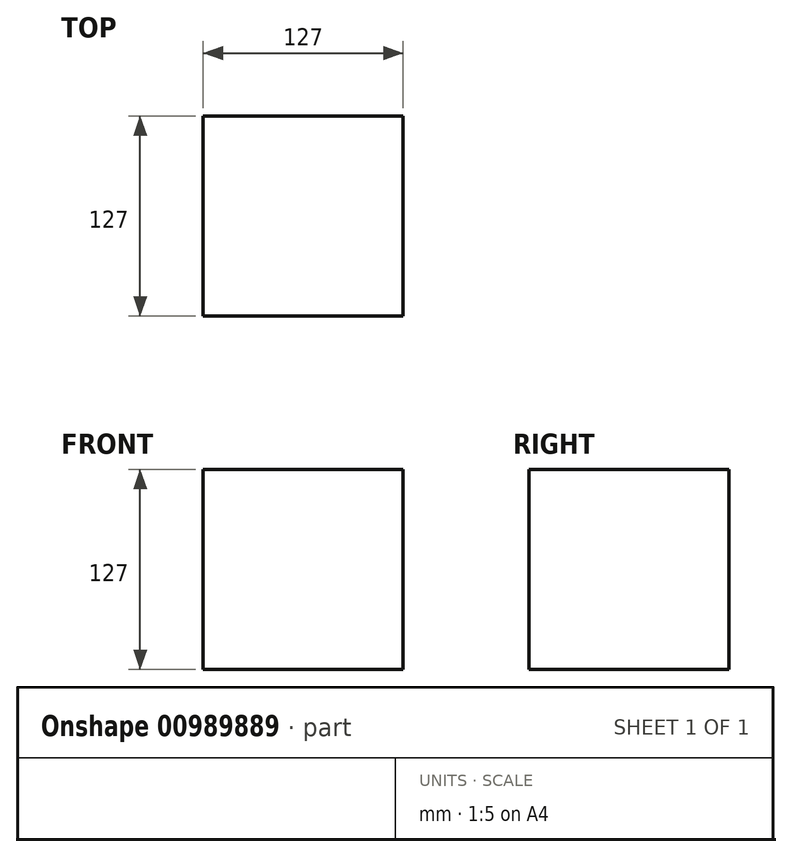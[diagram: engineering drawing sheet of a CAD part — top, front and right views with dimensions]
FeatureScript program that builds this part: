
annotation { "Feature Type Name" : "Feature", "Feature Type Description" : "" }
export const myFeature = defineFeature(function(context is Context, id is Id, definition is map)
    precondition{}
    {
        {
            var Q0;
            Q0=qCreatedBy(makeId("Top.planeOp"),FACE);
            var sketch = newSketch(context, id + "F0", { "sketchPlane" : qUnion([Q0])});
            skLineSegment(sketch, "E0.bottom", {"start": v(0, 0) * mm, "end": v(127, 0) * mm});
            skLineSegment(sketch, "E0.top", {"start": v(0, 127) * mm, "end": v(127, 127) * mm});
            skLineSegment(sketch, "E0.left", {"start": v(0, 0) * mm, "end": v(0, 127) * mm});
            skLineSegment(sketch, "E0.right", {"start": v(127, 0) * mm, "end": v(127, 127) * mm});
            skSolve(sketch);
        }
        {
            var Q0;
            Q0=makeQuery(id+"F0.imprint","IMPRINT",FACE,{"disambiguationData":[TD([[makeQuery(id+"F0.imprint","IMPRINT",EDGE,{"derivedFrom":sQuery(id+"F0.wireOp",EDGE,"E0.bottom")}),1.0]])]});
            extrude(context, id + "F1", {"entities" : qUnion([Q0]), "depth" : 127 * mm, "offsetDistance" : 25.4 * mm});
        }
    });
